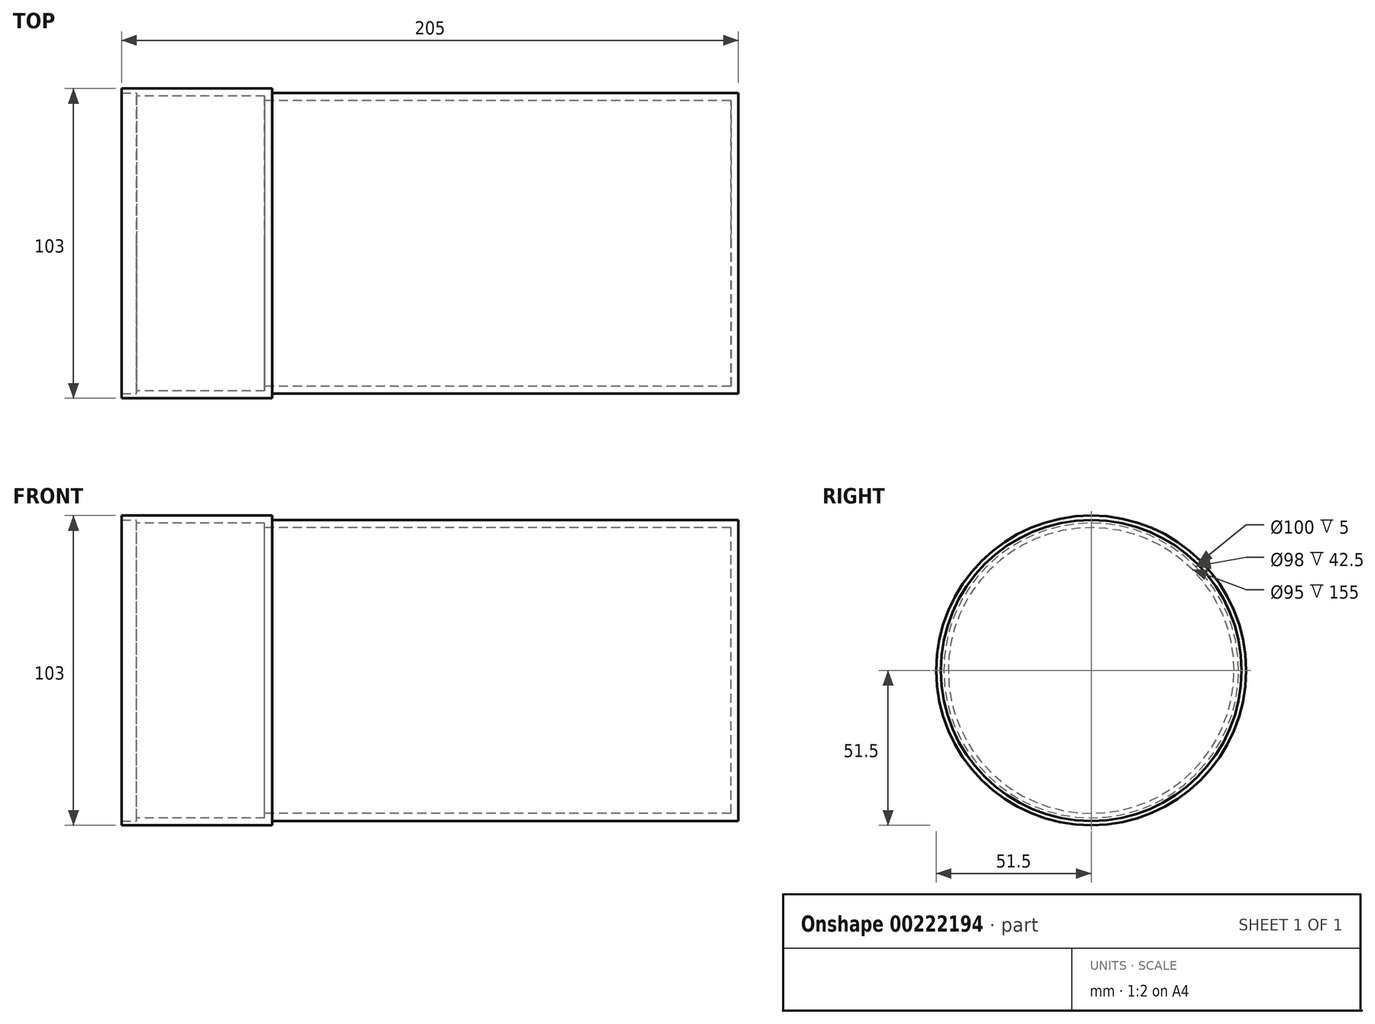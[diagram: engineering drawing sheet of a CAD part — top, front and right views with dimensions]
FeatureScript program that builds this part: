
annotation { "Feature Type Name" : "Feature", "Feature Type Description" : "" }
export const myFeature = defineFeature(function(context is Context, id is Id, definition is map)
    precondition{}
    {
        {
            var Q0;
            Q0=qCreatedBy(makeId("Right.planeOp"),FACE);
            var sketch = newSketch(context, id + "F0", { "sketchPlane" : qUnion([Q0])});
            skCircle(sketch, "E0", {"center": v(0, 0) * mm, "radius": 51.5 * mm});
            skCircle(sketch, "E1", {"center": v(0, 0) * mm, "radius": 50 * mm});
            skSolve(sketch);
        }
        {
            var Q0;
            Q0=makeQuery(id+"F0.imprint","IMPRINT",FACE,{"disambiguationData":[TD([[makeQuery(id+"F0.imprint","IMPRINT",EDGE,{"derivedFrom":sQuery(id+"F0.wireOp",EDGE,"E0")}),1.0]])]});
            extrude(context, id + "F1", {"entities" : qUnion([Q0]), "depth" : 45 * mm});
        }
        {
            var Q0;
            Q0=makeQuery(id+"F0.imprint","IMPRINT",FACE,{"disambiguationData":[TD([[makeQuery(id+"F0.imprint","IMPRINT",EDGE,{"derivedFrom":sQuery(id+"F0.wireOp",EDGE,"E1")}),1.0]])]});
            extrude(context, id + "F2", {"entities" : qUnion([Q0]), "operationType" : NewBodyOperationType.ADD, "depth" : 200 * mm});
        }
        {
            var Q0;
            Q0=makeQuery(id+"F0.imprint","IMPRINT",FACE,{"disambiguationData":[TD([[makeQuery(id+"F0.imprint","IMPRINT",EDGE,{"derivedFrom":sQuery(id+"F0.wireOp",EDGE,"E0")}),1.0]])]});
            extrude(context, id + "F3", {"entities" : qUnion([Q0]), "operationType" : NewBodyOperationType.ADD, "oppositeDirection" : true, "depth" : 5 * mm});
        }
        {
            var Q0;
            {var subQ0=sQuery(id+"F0.wireOp",EDGE,"E1");Q0=makeQuery(id+"F2.boolean.opBoolean","MERGE",FACE,{"derivedFrom":[makeQuery(id+"F1.opExtrude","CAP_FACE",FACE,{"disambiguationData":[OSD([sQuery(id+"F0.wireOp",EDGE,"E0"),subQ0])],"isStart":true}),makeQuery(id+"F2.opExtrude","CAP_FACE",FACE,{"disambiguationData":[OSD([subQ0])],"isStart":true})]});}
            shell(context, id + "F4", {"entities" : qUnion([Q0]), "thickness" : 2.5 * mm});
        }
    });
